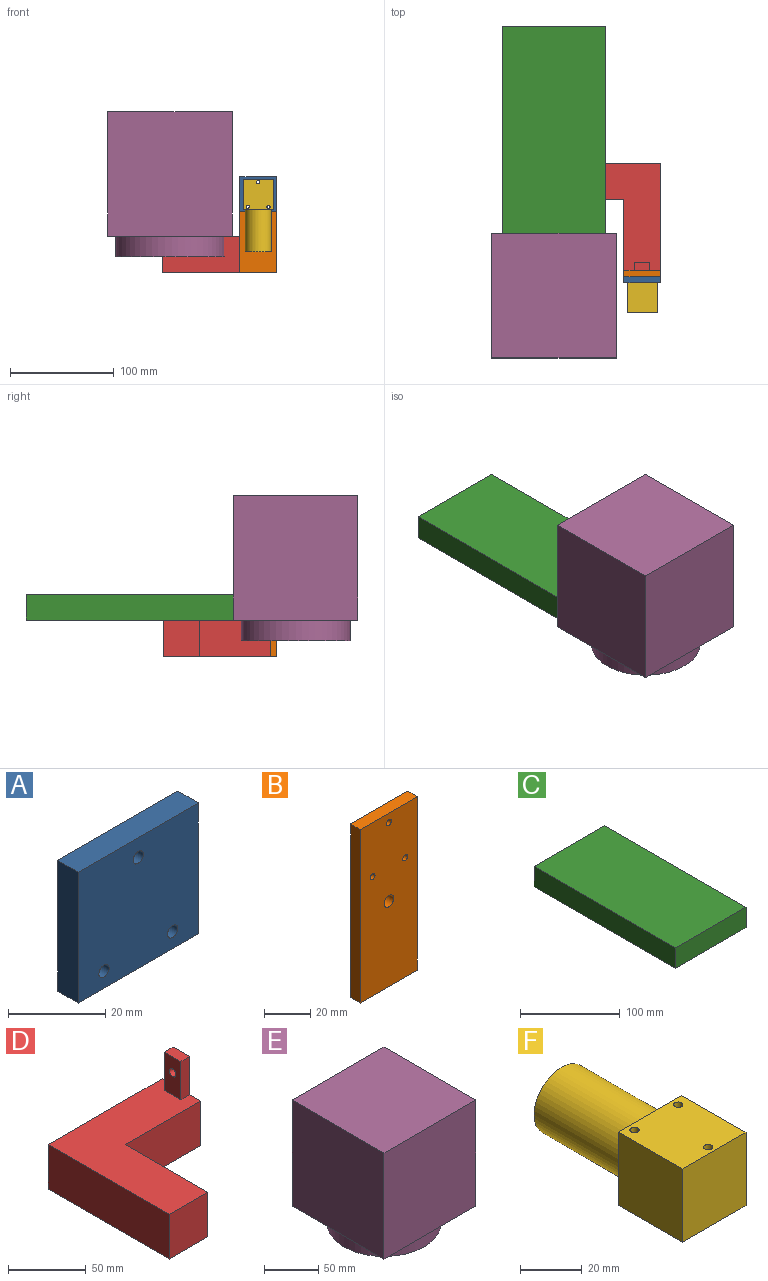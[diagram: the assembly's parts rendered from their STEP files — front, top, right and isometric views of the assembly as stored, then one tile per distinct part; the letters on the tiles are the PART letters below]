
ASSEMBLY  parts=6 mates=5
PART A: 9 faces, bbox 35x6x33 mm
  f0: plane 35x6mm, normal (0,0,-1), area 210mm2, adj f1,f6,f7,f8
  f1: plane 33x6mm, normal (1,0,0), area 198mm2, adj f0,f2,f7,f8
  f2: plane 35x6mm, normal (0,0,1), area 210mm2, adj f1,f6,f7,f8
  f3: cylinder r=1.5mm len=6mm, axis (0,1,0), area 56.5mm2, adj f7,f8
  f4: cylinder r=1.5mm len=6mm, axis (0,1,0), area 56.5mm2, adj f7,f8
  f5: cylinder r=1.5mm len=6mm, axis (0,1,0), area 56.5mm2, adj f7,f8
  f6: plane 33x6mm, normal (-1,0,0), area 198mm2, adj f0,f2,f7,f8
  f7: plane 35x33mm, normal (0,-1,0), area 1133.8mm2, adj f0,f1,f2,f3,f4,f5,f6
  f8: plane 35x33mm, normal (0,1,0), area 1133.8mm2, adj f0,f1,f2,f3,f4,f5,f6
PART B: 10 faces, bbox 35x6x92 mm
  f0: plane 35x6mm, normal (0,0,-1), area 210mm2, adj f1,f7,f8,f9
  f1: plane 92x6mm, normal (1,0,0), area 552mm2, adj f0,f2,f8,f9
  f2: plane 35x6mm, normal (0,0,1), area 210mm2, adj f1,f7,f8,f9
  f3: cylinder r=1.5mm len=6mm, axis (0,1,0), area 56.5mm2, adj f8,f9
  f4: cylinder r=1.5mm len=6mm, axis (0,1,0), area 56.5mm2, adj f8,f9
  f5: cylinder r=1.5mm len=6mm, axis (0,1,0), area 56.5mm2, adj f8,f9
  f6: cylinder r=3mm len=6mm, axis (0,1,0), area 113.1mm2, adj f8,f9
  f7: plane 92x6mm, normal (-1,0,0), area 552mm2, adj f0,f2,f8,f9
  f8: plane 92x35mm, normal (0,-1,0), area 3170.5mm2, adj f0,f1,f2,f3,f4,f5,f6,f7
  f9: plane 92x35mm, normal (0,1,0), area 3170.5mm2, adj f0,f1,f2,f3,f4,f5,f6,f7
PART C: 6 faces, bbox 100x200x25 mm
  f0: plane 100x25mm, normal (0,-1,0), area 2500mm2, adj f1,f3,f4,f5
  f1: plane 200x25mm, normal (1,0,0), area 5000mm2, adj f0,f2,f4,f5
  f2: plane 100x25mm, normal (0,1,0), area 2500mm2, adj f1,f3,f4,f5
  f3: plane 200x25mm, normal (-1,0,0), area 5000mm2, adj f0,f2,f4,f5
  f4: plane 200x100mm, normal (0,0,1), area 20000mm2, adj f0,f1,f2,f3
  f5: plane 200x100mm, normal (0,0,-1), area 20000mm2, adj f0,f1,f2,f3
PART D: 13 faces, bbox 103.5x110x65 mm
  f0: plane 110x103.5mm, normal (0,0,1), area 6127.5mm2, adj f1,f2,f3,f4,f5,f6,f8,f9
  f1: plane 110x35mm, normal (-1,0,0), area 3850mm2, adj f0,f2,f6,f7
  f2: plane 35x35mm, normal (0,-1,0), area 1225mm2, adj f0,f1,f3,f7
  f3: plane 75x35mm, normal (1,0,0), area 2625mm2, adj f0,f2,f4,f7
  f4: plane 68.5x35mm, normal (0,-1,0), area 2397.5mm2, adj f0,f3,f5,f7
  f5: plane 65x35mm, normal (1,0,0), area 1646.7mm2, adj f0,f4,f6,f7,f9,f10,f11,f12
  f6: plane 103.5x35mm, normal (0,1,0), area 3622.5mm2, adj f0,f1,f5,f7
  f7: plane 110x103.5mm, normal (0,0,-1), area 6247.5mm2, adj f1,f2,f3,f4,f5,f6
  f8: plane 30x15mm, normal (-1,0,0), area 421.7mm2, adj f0,f9,f10,f11,f12
  f9: plane 30x8mm, normal (0,-1,0), area 240mm2, adj f0,f5,f8,f11
  f10: plane 30x8mm, normal (0,1,0), area 240mm2, adj f0,f5,f8,f11
  f11: plane 15x8mm, normal (0,0,1), area 120mm2, adj f5,f8,f9,f10
  f12: cylinder r=3mm len=8mm, axis (1,0,0), area 150.8mm2, adj f5,f8
PART E: 8 faces, bbox 120x120x140 mm
  f0: plane 120x120mm, normal (0,0,-1), area 5741mm2, adj f1,f3,f4,f5,f6
  f1: plane 120x120mm, normal (1,0,0), area 14400mm2, adj f0,f2,f4,f5
  f2: plane 120x120mm, normal (0,0,1), area 14400mm2, adj f1,f3,f4,f5
  f3: plane 120x120mm, normal (-1,0,0), area 14400mm2, adj f0,f2,f4,f5
  f4: plane 120x120mm, normal (0,-1,0), area 14400mm2, adj f0,f1,f2,f3
  f5: plane 120x120mm, normal (0,1,0), area 14400mm2, adj f0,f1,f2,f3
  f6: cylinder r=52.5mm len=105mm, axis (0,0,1), area 6597.3mm2, adj f0,f7
  f7: plane 105x105mm, normal (0,0,-1), area 8659mm2, adj f6
PART F: 11 faces, bbox 29x70x29 mm
  f0: plane 29x29mm, normal (0,-1,0), area 841mm2, adj f1,f6,f7,f8
  f1: plane 29.3x29mm, normal (1,0,0), area 849.7mm2, adj f0,f2,f7,f8
  f2: plane 29x29mm, normal (0,1,0), area 350.1mm2, adj f1,f6,f7,f8,f9
  f3: cylinder r=1.5mm len=29mm, axis (0,0,-1), area 273.3mm2, adj f7,f8
  f4: cylinder r=1.5mm len=29mm, axis (0,0,-1), area 273.3mm2, adj f7,f8
  f5: cylinder r=1.5mm len=29mm, axis (0,0,-1), area 273.3mm2, adj f7,f8
  f6: plane 29.3x29mm, normal (-1,0,0), area 849.7mm2, adj f0,f2,f7,f8
  f7: plane 29.3x29mm, normal (0,0,1), area 828.5mm2, adj f0,f1,f2,f3,f4,f5,f6
  f8: plane 29.3x29mm, normal (0,0,-1), area 828.5mm2, adj f0,f1,f2,f3,f4,f5,f6
  f9: cylinder r=12.5mm len=40.7mm, axis (0,-1,0), area 3196.6mm2, adj f2,f10
  f10: plane 25x25mm, normal (0,1,0), area 490.9mm2, adj f9
PLACE A rot(axis=(0,1,0),0deg) t=(183.04,-104.43,166.4)mm
PLACE B rot(axis=(0,0.98,-0.2),0deg) t=(200.54,-98.43,120.4)mm
PLACE C t=(115.59,37.16,109.4)mm
PLACE D rot(axis=(0,0,-1),90deg) t=(183.04,5.07,74.4)mm
PLACE E rot(axis=(1,0,0),0deg) t=(115.59,-62.84,169.4)mm
PLACE F rot(axis=(0,-0.71,0.71),180deg) t=(200.54,-110.43,149.55)mm
MATE planar D.f0 <-> C.f5  axis (0,0,1) through (183.04,-29.93,109.4)mm
MATE fastened B.f0 <-> D.f7  axis (0,0,-1) through (200.54,-98.43,74.4)mm
MATE fastened A.f3 <-> B.f3  axis (0,1,0) through (200.54,-104.43,161.4)mm
MATE fastened A.f3 <-> F.f3  axis (0,-1,0) through (200.54,-110.43,161.4)mm
MATE fastened E.f5 <-> C.f0  axis (0,1,0) through (115.59,-62.84,109.4)mm
